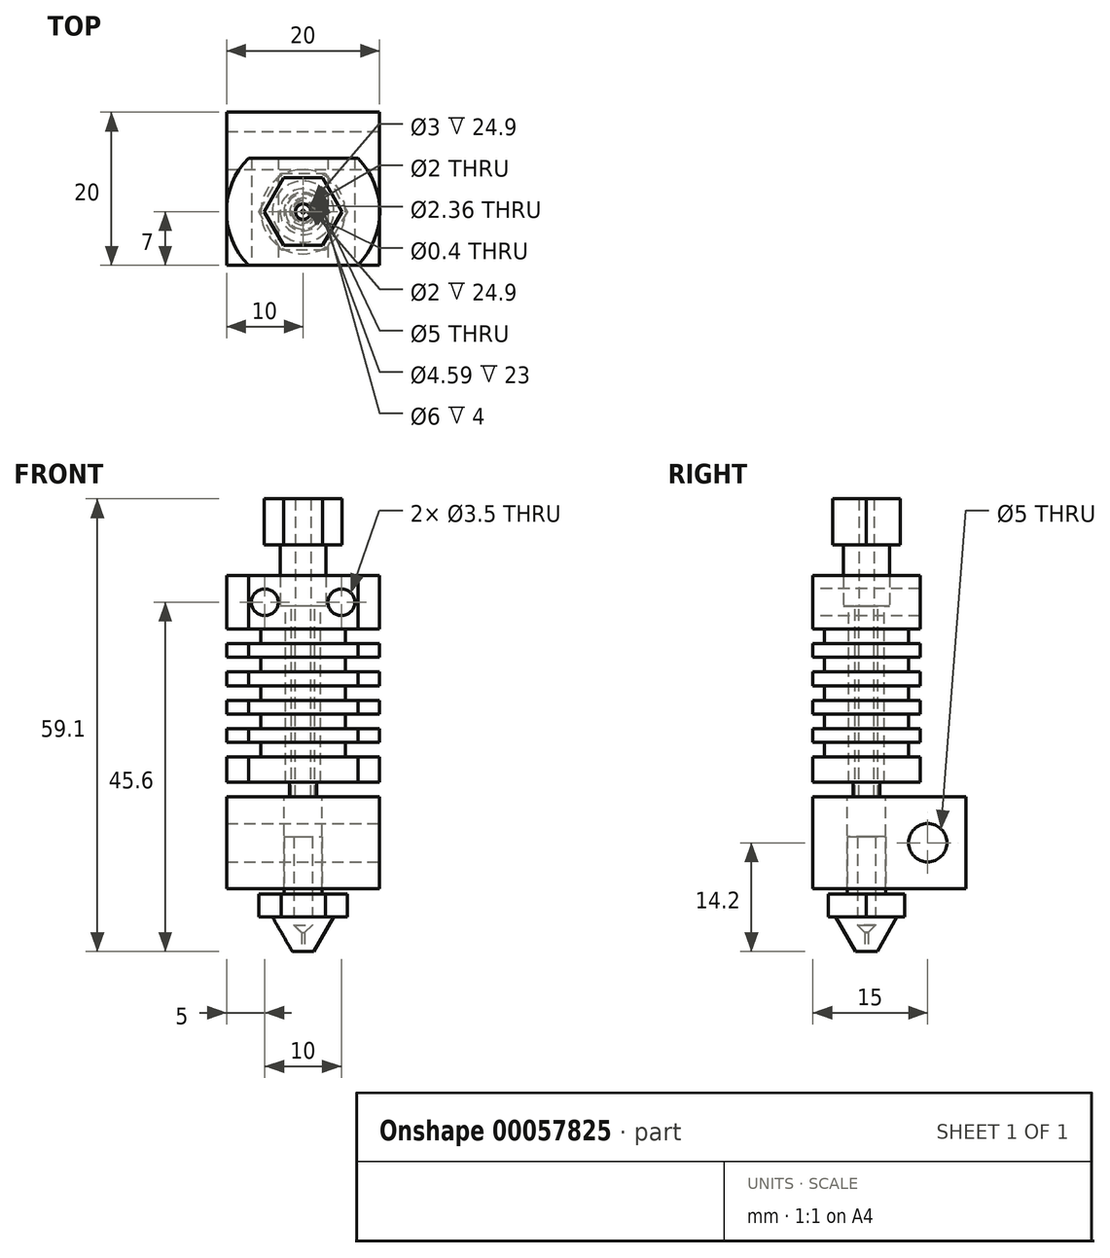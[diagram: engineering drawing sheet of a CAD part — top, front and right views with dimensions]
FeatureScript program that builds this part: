
annotation { "Feature Type Name" : "Feature", "Feature Type Description" : "" }
export const myFeature = defineFeature(function(context is Context, id is Id, definition is map)
    precondition{}
    {
        {
            var Q0;
            Q0=qCreatedBy(makeId("Top.planeOp"),FACE);
            var sketch = newSketch(context, id + "F0", { "sketchPlane" : qUnion([Q0])});
            skCircle(sketch, "E0", {"center": v(0, 0) * mm, "radius": 10 * mm});
            skLineSegment(sketch, "E1", {"start": v(-7.14, 7) * mm, "end": v(7.14, 7) * mm});
            skLineSegment(sketch, "E2", {"start": v(-7.14, -7) * mm, "end": v(7.14, -7) * mm});
            skLineSegment(sketch, "E3", {"start": v(0, 0) * mm, "end": v(-32.19, 0) * mm, "construction": true});
            skCircle(sketch, "E4", {"center": v(0, 0) * mm, "radius": 2.3 * mm});
            skSolve(sketch);
        }
        {
            var Q0;
            {var subQ0=sQuery(id+"F0.wireOp",EDGE,"E1");Q0=makeQuery(id+"F0.imprint","IMPRINT",FACE,{"disambiguationData":[TD([[makeQuery(id+"F0.imprint","IMPRINT",EDGE,{"derivedFrom":subQ0}),-1.0]])]});}
            extrude(context, id + "F1", {"entities" : qUnion([Q0]), "oppositeDirection" : true, "depth" : 27 * mm, "offsetDistance" : 25 * mm});
        }
        {
            var Q0;
            Q0=qCreatedBy(makeId("Front.planeOp"),FACE);
            var sketch = newSketch(context, id + "F2", { "sketchPlane" : qUnion([Q0])});
            skCircle(sketch, "E5", {"center": v(-5, -3.5) * mm, "radius": 1.75 * mm});
            skCircle(sketch, "E6", {"center": v(5, -3.5) * mm, "radius": 1.75 * mm});
            skLineSegment(sketch, "E7.bottom", {"start": v(-5.5, -7) * mm, "end": v(-15.5, -7) * mm});
            skLineSegment(sketch, "E7.top", {"start": v(-5.5, -8.9) * mm, "end": v(-15.5, -8.9) * mm});
            skLineSegment(sketch, "E7.left", {"start": v(-5.5, -7) * mm, "end": v(-5.5, -8.9) * mm});
            skLineSegment(sketch, "E7.right", {"start": v(-15.5, -7) * mm, "end": v(-15.5, -8.9) * mm});
            skLineSegment(sketch, "E8", {"start": v(0, 0) * mm, "end": v(0, 25.89) * mm, "construction": true});
            skLineSegment(sketch, "E9", {"start": v(0, 0) * mm, "end": v(-31.96, 0) * mm, "construction": true});
            skLineSegment(sketch, "E10.0.1.0", {"start": v(-5.5, -10.7) * mm, "end": v(-15.5, -10.7) * mm});
            skLineSegment(sketch, "E10.0.1.1", {"start": v(-5.5, -12.6) * mm, "end": v(-15.5, -12.6) * mm});
            skLineSegment(sketch, "E10.0.1.2", {"start": v(-5.5, -10.7) * mm, "end": v(-5.5, -12.6) * mm});
            skLineSegment(sketch, "E10.0.1.3", {"start": v(-15.5, -10.7) * mm, "end": v(-15.5, -12.6) * mm});
            skLineSegment(sketch, "E10.direction1", {"start": v(-15.5, -8.9) * mm, "end": v(9.5, -8.9) * mm, "construction": true});
            skLineSegment(sketch, "E10.direction2", {"start": v(-15.5, -8.9) * mm, "end": v(-15.5, -12.6) * mm, "construction": true});
            skLineSegment(sketch, "E11.0.0.2", {"start": v(-5.5, -14.4) * mm, "end": v(-15.5, -14.4) * mm});
            skLineSegment(sketch, "E11.3.0.2", {"start": v(-5.5, -16.3) * mm, "end": v(-15.5, -16.3) * mm});
            skLineSegment(sketch, "E11.6.0.2", {"start": v(-5.5, -14.4) * mm, "end": v(-5.5, -16.3) * mm});
            skLineSegment(sketch, "E11.9.0.2", {"start": v(-15.5, -14.4) * mm, "end": v(-15.5, -16.3) * mm});
            skLineSegment(sketch, "E12.0.0.3", {"start": v(-5.5, -18.1) * mm, "end": v(-15.5, -18.1) * mm});
            skLineSegment(sketch, "E12.3.0.3", {"start": v(-5.5, -20) * mm, "end": v(-15.5, -20) * mm});
            skLineSegment(sketch, "E12.6.0.3", {"start": v(-5.5, -18.1) * mm, "end": v(-5.5, -20) * mm});
            skLineSegment(sketch, "E12.9.0.3", {"start": v(-15.5, -18.1) * mm, "end": v(-15.5, -20) * mm});
            skLineSegment(sketch, "E13.0.0.4", {"start": v(-5.5, -21.8) * mm, "end": v(-15.5, -21.8) * mm});
            skLineSegment(sketch, "E13.3.0.4", {"start": v(-5.5, -23.7) * mm, "end": v(-15.5, -23.7) * mm});
            skLineSegment(sketch, "E13.6.0.4", {"start": v(-5.5, -21.8) * mm, "end": v(-5.5, -23.7) * mm});
            skLineSegment(sketch, "E13.9.0.4", {"start": v(-15.5, -21.8) * mm, "end": v(-15.5, -23.7) * mm});
            skSolve(sketch);
        }
        {
            var Q0;
            Q0=makeQuery(id+"F2.imprint","IMPRINT",FACE,{"disambiguationData":[TD([[makeQuery(id+"F2.imprint","IMPRINT",EDGE,{"derivedFrom":sQuery(id+"F2.wireOp",EDGE,"E7.bottom")}),1.0]])]});
            var Q1;
            Q1=makeQuery(id+"F2.imprint","IMPRINT",FACE,{"disambiguationData":[TD([[makeQuery(id+"F2.imprint","IMPRINT",EDGE,{"derivedFrom":sQuery(id+"F2.wireOp",EDGE,"E10.0.1.0")}),1.0]])]});
            var Q2;
            Q2=makeQuery(id+"F2.imprint","IMPRINT",FACE,{"disambiguationData":[TD([[makeQuery(id+"F2.imprint","IMPRINT",EDGE,{"derivedFrom":sQuery(id+"F2.wireOp",EDGE,"E11.0.0.2")}),1.0]])]});
            var Q3;
            Q3=makeQuery(id+"F2.imprint","IMPRINT",FACE,{"disambiguationData":[TD([[makeQuery(id+"F2.imprint","IMPRINT",EDGE,{"derivedFrom":sQuery(id+"F2.wireOp",EDGE,"E12.0.0.3")}),1.0]])]});
            var Q4;
            Q4=makeQuery(id+"F2.imprint","IMPRINT",FACE,{"disambiguationData":[TD([[makeQuery(id+"F2.imprint","IMPRINT",EDGE,{"derivedFrom":sQuery(id+"F2.wireOp",EDGE,"E13.0.0.4")}),1.0]])]});
            var Q5;
            Q5=sQuery(id+"F2.wireOp",EDGE,"E8");
            revolve(context, id + "F3", {"operationType" : NewBodyOperationType.REMOVE, "entities" : qUnion([Q0, Q1, Q2, Q3, Q4]), "axis" : qUnion([Q5]), "revolveType" : RevolveType.FULL, "oppositeDirection" : true});
        }
        {
            var Q0;
            Q0=makeQuery(id+"F2.imprint","IMPRINT",FACE,{"disambiguationData":[TD([[makeQuery(id+"F2.imprint","IMPRINT",EDGE,{"derivedFrom":sQuery(id+"F2.wireOp",EDGE,"E5")}),1.0]])]});
            var Q1;
            Q1=makeQuery(id+"F2.imprint","IMPRINT",FACE,{"disambiguationData":[TD([[makeQuery(id+"F2.imprint","IMPRINT",EDGE,{"derivedFrom":sQuery(id+"F2.wireOp",EDGE,"E6")}),1.0]])]});
            extrude(context, id + "F4", {"entities" : qUnion([Q0, Q1]), "operationType" : NewBodyOperationType.REMOVE, "endBound" : BoundingType.SYMMETRIC, "oppositeDirection" : true, "depth" : 25 * mm, "offsetDistance" : 25 * mm});
        }
        {
            var Q0;
            Q0=makeQuery(id+"F1.opExtrude","CAP_FACE",FACE,{"disambiguationData":[OSD([sQuery(id+"F0.wireOp",EDGE,"E0"),sQuery(id+"F0.wireOp",EDGE,"E1"),sQuery(id+"F0.wireOp",EDGE,"E2"),sQuery(id+"F0.wireOp",EDGE,"E4")])],"isStart":true});
            var sketch = newSketch(context, id + "F5", { "sketchPlane" : qUnion([Q0])});
            skCircle(sketch, "E14", {"center": v(0, 0) * mm, "radius": 3 * mm});
            skSolve(sketch);
        }
        {
            var Q0;
            Q0 = qSketchRegion(id + "F5", true);
            extrude(context, id + "F6", {"entities" : qUnion([Q0]), "operationType" : NewBodyOperationType.REMOVE, "oppositeDirection" : true, "depth" : 4 * mm, "offsetDistance" : 25 * mm});
        }
        {
            var Q0;
            Q0=makeQuery(id+"F6.boolean.opBoolean","COPY",FACE,{"derivedFrom":makeQuery(id+"F6.opExtrude","CAP_FACE",FACE,{"disambiguationData":[OSD([sQuery(id+"F5.wireOp",EDGE,"E14")])],"isStart":false})});
            var sketch = newSketch(context, id + "F7", { "sketchPlane" : qUnion([Q0])});
            skCircle(sketch, "E15", {"center": v(0, 0) * mm, "radius": 1 * mm});
            skCircle(sketch, "E16", {"center": v(0, 0) * mm, "radius": 1.5 * mm});
            skCircle(sketch, "E17.0", {"center": v(0, 0) * mm, "radius": 2.3 * mm});
            skSolve(sketch);
        }
        {
            var Q0;
            Q0 = qSketchRegion(id + "F7", true);
            extrude(context, id + "F8", {"entities" : qUnion([Q0]), "oppositeDirection" : true, "depth" : 30 * mm, "offsetDistance" : 25 * mm});
        }
        {
            var Q0;
            Q0=makeQuery(id+"F7.imprint","IMPRINT",FACE,{"disambiguationData":[TD([[makeQuery(id+"F7.imprint","IMPRINT",EDGE,{"derivedFrom":sQuery(id+"F7.wireOp",EDGE,"E15")}),-1.0]])]});
            var Q1;
            Q1=makeQuery(id+"F8.opExtrude","CAP_FACE",FACE,{"disambiguationData":[OSD([sQuery(id+"F7.wireOp",EDGE,"E16"),sQuery(id+"F7.wireOp",EDGE,"E17.0")])],"isStart":false});
            extrude(context, id + "F9", {"entities" : qUnion([Q0]), "endBound" : BoundingType.UP_TO_SURFACE, "oppositeDirection" : true, "depth" : 25 * mm, "endBoundEntityFace" : qUnion([Q1]), "offsetDistance" : 25 * mm});
        }
        {
            var Q0;
            Q0=qCreatedBy(makeId("Front.planeOp"),FACE);
            var sketch = newSketch(context, id + "F10", { "sketchPlane" : qUnion([Q0])});
            skLineSegment(sketch, "E18.bottom", {"start": v(-11.75, -27) * mm, "end": v(-1.75, -27) * mm});
            skLineSegment(sketch, "E18.top", {"start": v(-11.75, -29.5) * mm, "end": v(-1.75, -29.5) * mm});
            skLineSegment(sketch, "E18.left", {"start": v(-11.75, -27) * mm, "end": v(-11.75, -29.5) * mm});
            skLineSegment(sketch, "E18.right", {"start": v(-1.75, -27) * mm, "end": v(-1.75, -29.5) * mm});
            skLineSegment(sketch, "E19", {"start": v(0, 0) * mm, "end": v(0, 19.5) * mm});
            skLineSegment(sketch, "E20.0", {"start": v(-7.14, -27) * mm, "end": v(7.14, -27) * mm});
            skSolve(sketch);
        }
        {
            var Q0;
            Q0=makeQuery(id+"F10.imprint","IMPRINT",FACE,{"disambiguationData":[TD([[makeQuery(id+"F10.imprint","IMPRINT",EDGE,{"derivedFrom":sQuery(id+"F10.wireOp",EDGE,"E18.bottom")}),-1.0]])]});
            var Q1;
            Q1=sQuery(id+"F10.wireOp",EDGE,"E19");
            revolve(context, id + "F11", {"operationType" : NewBodyOperationType.REMOVE, "entities" : qUnion([Q0]), "axis" : qUnion([Q1]), "revolveType" : RevolveType.FULL, "oppositeDirection" : true});
        }
        {
            var Q0;
            Q0=qCreatedBy(makeId("Front.planeOp"),FACE);
            var sketch = newSketch(context, id + "F12", { "sketchPlane" : qUnion([Q0])});
            skLineSegment(sketch, "E21.bottom", {"start": v(-10, -28.9) * mm, "end": v(10, -28.9) * mm});
            skLineSegment(sketch, "E21.top", {"start": v(-10, -40.9) * mm, "end": v(10, -40.9) * mm});
            skLineSegment(sketch, "E21.left", {"start": v(-10, -28.9) * mm, "end": v(-10, -40.9) * mm});
            skLineSegment(sketch, "E21.right", {"start": v(10, -28.9) * mm, "end": v(10, -40.9) * mm});
            skSolve(sketch);
        }
        {
            var Q0;
            Q0=makeQuery(id+"F12.imprint","IMPRINT",FACE,{"disambiguationData":[TD([[makeQuery(id+"F12.imprint","IMPRINT",EDGE,{"derivedFrom":sQuery(id+"F12.wireOp",EDGE,"E21.bottom")}),-1.0]])]});
            extrude(context, id + "F13", {"entities" : qUnion([Q0]), "depth" : 7 * mm, "offsetDistance" : 25 * mm, "hasSecondDirection" : true, "secondDirectionOppositeDirection" : true, "secondDirectionDepth" : 13 * mm});
        }
        {
            var Q0;
            Q0=makeQuery(id+"F13.opExtrude","SWEPT_FACE",FACE,{"disambiguationData":[OSD([sQuery(id+"F12.wireOp",EDGE,"E21.bottom")])]});
            var sketch = newSketch(context, id + "F14", { "sketchPlane" : qUnion([Q0])});
            skCircle(sketch, "E22", {"center": v(0, 0) * mm, "radius": 2.5 * mm});
            skSolve(sketch);
        }
        {
            var Q0;
            Q0=makeQuery(id+"F14.imprint","IMPRINT",FACE,{"disambiguationData":[TD([[makeQuery(id+"F14.imprint","IMPRINT",EDGE,{"derivedFrom":sQuery(id+"F14.wireOp",EDGE,"E22")}),1.0]])]});
            extrude(context, id + "F15", {"entities" : qUnion([Q0]), "operationType" : NewBodyOperationType.REMOVE, "endBound" : BoundingType.THROUGH_ALL, "oppositeDirection" : true, "depth" : 25 * mm, "offsetDistance" : 25 * mm});
        }
        {
            var Q0;
            Q0=makeQuery(id+"F13.opExtrude","SWEPT_FACE",FACE,{"disambiguationData":[OSD([sQuery(id+"F12.wireOp",EDGE,"E21.right")])]});
            var sketch = newSketch(context, id + "F16", { "sketchPlane" : qUnion([Q0])});
            skCircle(sketch, "E23", {"center": v(8, -34.9) * mm, "radius": 2.5 * mm});
            skLineSegment(sketch, "E24", {"start": v(8, -34.9) * mm, "end": v(13, -34.9) * mm});
            skLineSegment(sketch, "E25", {"start": v(0, 0) * mm, "end": v(0, 14.18) * mm});
            skSolve(sketch);
        }
        {
            var Q0;
            Q0=makeQuery(id+"F16.imprint","IMPRINT",FACE,{"disambiguationData":[TD([[makeQuery(id+"F16.imprint","IMPRINT",EDGE,{"derivedFrom":sQuery(id+"F16.wireOp",EDGE,"E23")}),1.0]])]});
            extrude(context, id + "F17", {"entities" : qUnion([Q0]), "operationType" : NewBodyOperationType.REMOVE, "endBound" : BoundingType.SYMMETRIC, "oppositeDirection" : true, "depth" : 40 * mm, "offsetDistance" : 25 * mm});
        }
        {
            var Q0;
            Q0=qCreatedBy(makeId("Right.planeOp"),FACE);
            var sketch = newSketch(context, id + "F18", { "sketchPlane" : qUnion([Q0])});
            skLineSegment(sketch, "E26", {"start": v(1.18, -34.1) * mm, "end": v(1.18, -45.66) * mm});
            skLineSegment(sketch, "E27", {"start": v(1.18, -45.66) * mm, "end": v(0.2, -46.64) * mm});
            skLineSegment(sketch, "E28", {"start": v(0.2, -46.64) * mm, "end": v(0.2, -49.1) * mm});
            skLineSegment(sketch, "E29", {"start": v(0.2, -49.1) * mm, "end": v(1.4, -49.1) * mm});
            skLineSegment(sketch, "E30", {"start": v(1.4, -49.1) * mm, "end": v(4, -44.6) * mm});
            skLineSegment(sketch, "E31", {"start": v(4, -44.6) * mm, "end": v(4, -41.6) * mm});
            skLineSegment(sketch, "E32", {"start": v(4, -41.6) * mm, "end": v(2.5, -41.6) * mm});
            skLineSegment(sketch, "E33", {"start": v(2.5, -41.6) * mm, "end": v(2.5, -34.1) * mm});
            skLineSegment(sketch, "E34", {"start": v(2.5, -34.1) * mm, "end": v(1.18, -34.1) * mm});
            skLineSegment(sketch, "E35", {"start": v(0, 0) * mm, "end": v(0, 9.17) * mm});
            skLineSegment(sketch, "E36.0", {"start": v(1, -34) * mm, "end": v(-1, -34) * mm});
            skSolve(sketch);
        }
        {
            var Q0;
            Q0=makeQuery(id+"F18.imprint","IMPRINT",FACE,{"disambiguationData":[TD([[makeQuery(id+"F18.imprint","IMPRINT",EDGE,{"derivedFrom":sQuery(id+"F18.wireOp",EDGE,"E26")}),1.0]])]});
            var Q1;
            Q1=sQuery(id+"F18.wireOp",EDGE,"E35");
            revolve(context, id + "F19", {"entities" : qUnion([Q0]), "axis" : qUnion([Q1]), "revolveType" : RevolveType.FULL});
        }
        {
            var Q0;
            Q0=makeQuery(id+"F19.opRevolve","SWEPT_FACE",FACE,{"disambiguationData":[OSD([sQuery(id+"F18.wireOp",EDGE,"E32")])]});
            var sketch = newSketch(context, id + "F20", { "sketchPlane" : qUnion([Q0])});
            skCircle(sketch, "E37.cCircle", {"center": v(0, 0) * mm, "radius": 5 * mm, "construction": true});
            skLineSegment(sketch, "E37.0", {"start": v(2.89, 5) * mm, "end": v(5.77, 0) * mm});
            skLineSegment(sketch, "E37.1", {"start": v(5.77, 0) * mm, "end": v(2.89, -5) * mm});
            skLineSegment(sketch, "E37.2", {"start": v(2.89, -5) * mm, "end": v(-2.89, -5) * mm});
            skLineSegment(sketch, "E37.3", {"start": v(-2.89, -5) * mm, "end": v(-5.77, 0) * mm});
            skLineSegment(sketch, "E37.4", {"start": v(-5.77, 0) * mm, "end": v(-2.89, 5) * mm});
            skLineSegment(sketch, "E37.5", {"start": v(-2.89, 5) * mm, "end": v(2.89, 5) * mm});
            skPoint(sketch, "E37.0.midPoint", {"position": v(4.33, 2.5) * mm});
            skCircle(sketch, "E38.0", {"center": v(0, 0) * mm, "radius": 4 * mm});
            skSolve(sketch);
        }
        {
            var Q0;
            Q0=makeQuery(id+"F20.imprint","IMPRINT",FACE,{"disambiguationData":[TD([[makeQuery(id+"F20.imprint","IMPRINT",EDGE,{"derivedFrom":sQuery(id+"F20.wireOp",EDGE,"E37.0")}),-1.0]])]});
            extrude(context, id + "F21", {"entities" : qUnion([Q0]), "operationType" : NewBodyOperationType.ADD, "oppositeDirection" : true, "depth" : 3 * mm, "offsetDistance" : 25 * mm});
        }
        {
            var Q0;
            Q0=makeQuery(id+"F6.boolean.opBoolean","COPY",FACE,{"derivedFrom":makeQuery(id+"F6.opExtrude","CAP_FACE",FACE,{"disambiguationData":[OSD([sQuery(id+"F5.wireOp",EDGE,"E14")])],"isStart":false})});
            var sketch = newSketch(context, id + "F22", { "sketchPlane" : qUnion([Q0])});
            skCircle(sketch, "E39.0", {"center": v(0, 0) * mm, "radius": 3 * mm});
            skCircle(sketch, "E40.0", {"center": v(0, 0) * mm, "radius": 1 * mm});
            skSolve(sketch);
        }
        {
            var Q0;
            Q0=makeQuery(id+"F22.imprint","IMPRINT",FACE,{"disambiguationData":[TD([[makeQuery(id+"F22.imprint","IMPRINT",EDGE,{"derivedFrom":sQuery(id+"F22.wireOp",EDGE,"E39.0")}),1.0]])]});
            var Q1;
            Q1=makeQuery(id+"F22.imprint","IMPRINT",FACE,{"disambiguationData":[TD([[makeQuery(id+"F22.imprint","IMPRINT",EDGE,{"derivedFrom":sQuery(id+"F22.wireOp",EDGE,"E40.0")}),-1.0]])]});
            extrude(context, id + "F23", {"entities" : qUnion([Q0, Q1]), "depth" : 14 * mm, "offsetDistance" : 25 * mm});
        }
        {
            var Q0;
            Q0=makeQuery(id+"F23.opExtrude","CAP_FACE",FACE,{"disambiguationData":[OSD([sQuery(id+"F22.wireOp",EDGE,"E39.0"),sQuery(id+"F22.wireOp",EDGE,"E40.0")])],"isStart":false});
            var sketch = newSketch(context, id + "F24", { "sketchPlane" : qUnion([Q0])});
            skCircle(sketch, "E41.cCircle", {"center": v(0, 0) * mm, "radius": 4.42 * mm, "construction": true});
            skLineSegment(sketch, "E41.0", {"start": v(-2.55, 4.42) * mm, "end": v(2.55, 4.42) * mm});
            skLineSegment(sketch, "E41.1", {"start": v(2.55, 4.42) * mm, "end": v(5.1, 0) * mm});
            skLineSegment(sketch, "E41.2", {"start": v(5.1, 0) * mm, "end": v(2.55, -4.42) * mm});
            skLineSegment(sketch, "E41.3", {"start": v(2.55, -4.42) * mm, "end": v(-2.55, -4.42) * mm});
            skLineSegment(sketch, "E41.4", {"start": v(-2.55, -4.42) * mm, "end": v(-5.1, 0) * mm});
            skLineSegment(sketch, "E41.5", {"start": v(-5.1, 0) * mm, "end": v(-2.55, 4.42) * mm});
            skPoint(sketch, "E41.0.midPoint", {"position": v(0, 4.42) * mm});
            skSolve(sketch);
        }
        {
            var Q0;
            Q0=makeQuery(id+"F24.imprint","IMPRINT",FACE,{"disambiguationData":[TD([[makeQuery(id+"F24.imprint","IMPRINT",EDGE,{"derivedFrom":sQuery(id+"F24.wireOp",EDGE,"E41.0")}),-1.0]])]});
            extrude(context, id + "F25", {"entities" : qUnion([Q0]), "operationType" : NewBodyOperationType.ADD, "oppositeDirection" : true, "depth" : 6 * mm, "offsetDistance" : 25 * mm});
        }
    });
